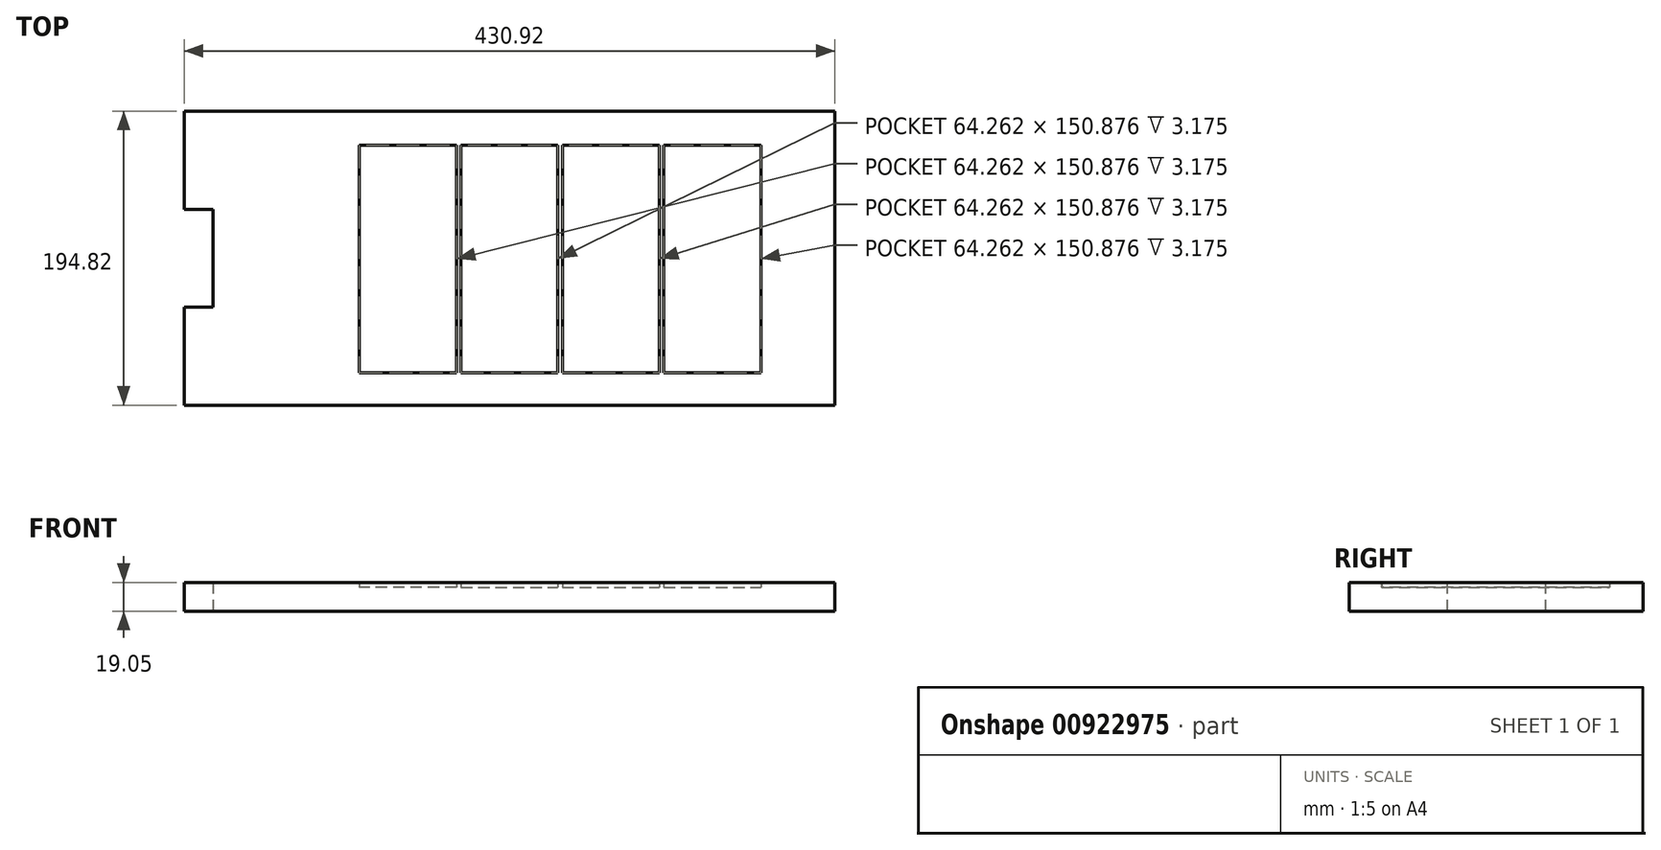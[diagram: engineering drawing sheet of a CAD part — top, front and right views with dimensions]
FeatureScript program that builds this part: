
annotation { "Feature Type Name" : "Feature", "Feature Type Description" : "" }
export const myFeature = defineFeature(function(context is Context, id is Id, definition is map)
    precondition{}
    {
        {
            var Q0;
            Q0=qCreatedBy(makeId("Top.planeOp"),FACE);
            var sketch = newSketch(context, id + "F0", { "sketchPlane" : qUnion([Q0])});
            skLineSegment(sketch, "E0.bottom", {"start": v(215.46, -97.4) * mm, "end": v(-215.46, -97.4) * mm});
            skLineSegment(sketch, "E0.top", {"start": v(215.46, 97.4) * mm, "end": v(-215.46, 97.4) * mm});
            skLineSegment(sketch, "E0.left", {"start": v(215.46, -97.4) * mm, "end": v(215.46, 97.4) * mm});
            skLineSegment(sketch, "E0.right", {"start": v(-215.46, -97.4) * mm, "end": v(-215.46, -32.47) * mm});
            skPoint(sketch, "E0.middle", {"position": v(0, 0) * mm});
            skLineSegment(sketch, "E1.bottom", {"start": v(-196.4, 78.36) * mm, "end": v(196.4, 78.36) * mm});
            skLineSegment(sketch, "E1.top", {"start": v(-196.4, -78.36) * mm, "end": v(196.4, -78.36) * mm});
            skLineSegment(sketch, "E1.left", {"start": v(-196.4, 78.36) * mm, "end": v(-196.4, -78.36) * mm});
            skLineSegment(sketch, "E1.right", {"start": v(196.4, 78.36) * mm, "end": v(196.4, -78.36) * mm});
            skPoint(sketch, "E2", {"position": v(-215.46, 0) * mm});
            skPoint(sketch, "E3", {"position": v(-215.46, 32.47) * mm});
            skPoint(sketch, "E4", {"position": v(-215.46, -32.47) * mm});
            skLineSegment(sketch, "E5.trimOffspring", {"start": v(-215.46, 32.47) * mm, "end": v(-215.46, 97.4) * mm});
            skLineSegment(sketch, "E6", {"start": v(-215.46, -32.47) * mm, "end": v(-196.4, -32.47) * mm});
            skLineSegment(sketch, "E7", {"start": v(-215.46, 32.47) * mm, "end": v(-196.4, 32.47) * mm});
            skLineSegment(sketch, "E8.bottom", {"start": v(-32.13, 75) * mm, "end": v(32.13, 75) * mm});
            skLineSegment(sketch, "E8.top", {"start": v(-32.13, -75.88) * mm, "end": v(32.13, -75.88) * mm});
            skLineSegment(sketch, "E8.left", {"start": v(-32.13, 75) * mm, "end": v(-32.13, -75.88) * mm});
            skLineSegment(sketch, "E8.right", {"start": v(32.13, 75) * mm, "end": v(32.13, -75.88) * mm});
            skPoint(sketch, "E8.middle", {"position": v(0, -0.44) * mm});
            skLineSegment(sketch, "E9.bottom", {"start": v(-35.05, -75.87) * mm, "end": v(-99.31, -75.87) * mm});
            skLineSegment(sketch, "E9.top", {"start": v(-35.05, 75) * mm, "end": v(-99.31, 75) * mm});
            skLineSegment(sketch, "E9.left", {"start": v(-35.05, -75.87) * mm, "end": v(-35.05, 75) * mm});
            skLineSegment(sketch, "E9.right", {"start": v(-99.31, -75.87) * mm, "end": v(-99.31, 75) * mm});
            skPoint(sketch, "E9.middle", {"position": v(-67.18, -0.43) * mm});
            skLineSegment(sketch, "E10.bottom", {"start": v(35.05, 75) * mm, "end": v(99.31, 75) * mm});
            skLineSegment(sketch, "E10.top", {"start": v(35.05, -75.87) * mm, "end": v(99.31, -75.87) * mm});
            skLineSegment(sketch, "E10.left", {"start": v(35.05, 75) * mm, "end": v(35.05, -75.87) * mm});
            skLineSegment(sketch, "E10.right", {"start": v(99.31, 75) * mm, "end": v(99.31, -75.87) * mm});
            skLineSegment(sketch, "E11.bottom", {"start": v(102.24, 75) * mm, "end": v(166.5, 75) * mm});
            skLineSegment(sketch, "E11.top", {"start": v(102.24, -75.87) * mm, "end": v(166.5, -75.87) * mm});
            skLineSegment(sketch, "E11.left", {"start": v(102.24, 75) * mm, "end": v(102.24, -75.87) * mm});
            skLineSegment(sketch, "E11.right", {"start": v(166.5, 75) * mm, "end": v(166.5, -75.87) * mm});
            skSolve(sketch);
        }
        {
            var Q0;
            Q0=makeQuery(id+"F0.imprint","IMPRINT",FACE,{"disambiguationData":[TD([[makeQuery(id+"F0.imprint","IMPRINT",EDGE,{"derivedFrom":sQuery(id+"F0.wireOp",EDGE,"E0.bottom")}),-1.0]])]});
            var Q1;
            {var subQ3=sQuery(id+"F0.wireOp",EDGE,"E1.bottom");Q1=makeQuery(id+"F0.imprint","IMPRINT",FACE,{"disambiguationData":[TD([[makeQuery(id+"F0.imprint","IMPRINT",EDGE,{"derivedFrom":subQ3}),-1.0]])]});}
            extrude(context, id + "F1", {"entities" : qUnion([Q0, Q1]), "depth" : 19.05 * mm, "offsetDistance" : 25.4 * mm});
        }
        {
            var Q0;
            Q0=makeQuery(id+"F0.imprint","IMPRINT",FACE,{"disambiguationData":[TD([[makeQuery(id+"F0.imprint","IMPRINT",EDGE,{"derivedFrom":sQuery(id+"F0.wireOp",EDGE,"E9.bottom")}),-1.0]])]});
            var Q1;
            Q1=makeQuery(id+"F0.imprint","IMPRINT",FACE,{"disambiguationData":[TD([[makeQuery(id+"F0.imprint","IMPRINT",EDGE,{"derivedFrom":sQuery(id+"F0.wireOp",EDGE,"E8.bottom")}),-1.0]])]});
            var Q2;
            Q2=makeQuery(id+"F0.imprint","IMPRINT",FACE,{"disambiguationData":[TD([[makeQuery(id+"F0.imprint","IMPRINT",EDGE,{"derivedFrom":sQuery(id+"F0.wireOp",EDGE,"E10.bottom")}),-1.0]])]});
            var Q3;
            Q3=makeQuery(id+"F0.imprint","IMPRINT",FACE,{"disambiguationData":[TD([[makeQuery(id+"F0.imprint","IMPRINT",EDGE,{"derivedFrom":sQuery(id+"F0.wireOp",EDGE,"E11.bottom")}),-1.0]])]});
            extrude(context, id + "F2", {"entities" : qUnion([Q0, Q1, Q2, Q3]), "operationType" : NewBodyOperationType.ADD, "depth" : 15.88 * mm, "offsetDistance" : 25.4 * mm});
        }
    });
